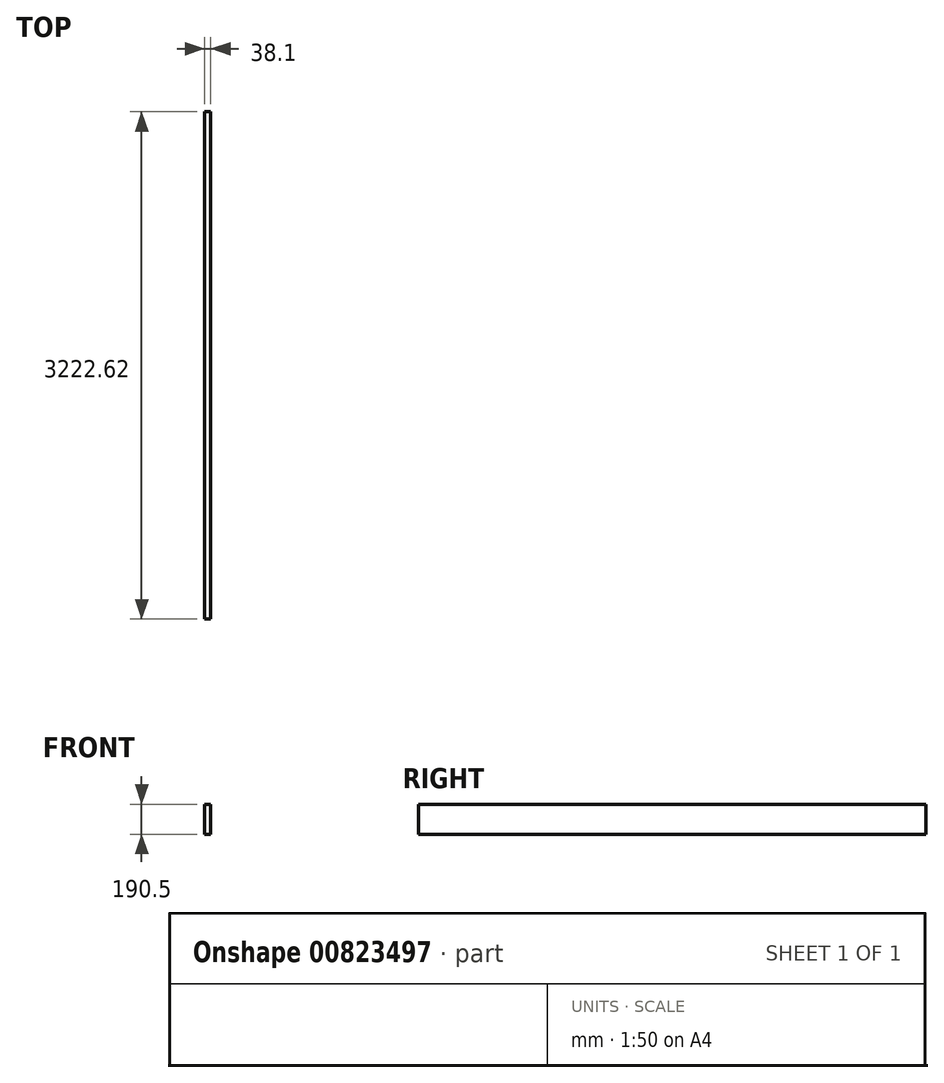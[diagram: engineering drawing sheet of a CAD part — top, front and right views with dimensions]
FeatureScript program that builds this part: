
annotation { "Feature Type Name" : "Feature", "Feature Type Description" : "" }
export const myFeature = defineFeature(function(context is Context, id is Id, definition is map)
    precondition{}
    {
        {
            var Q0;
            Q0=qCreatedBy(makeId("Front.planeOp"),FACE);
            var sketch = newSketch(context, id + "F0", { "sketchPlane" : qUnion([Q0])});
            skLineSegment(sketch, "E0.bottom", {"start": v(0, 0) * mm, "end": v(38.1, 0) * mm});
            skLineSegment(sketch, "E0.top", {"start": v(0, 190.5) * mm, "end": v(38.1, 190.5) * mm});
            skLineSegment(sketch, "E0.left", {"start": v(0, 0) * mm, "end": v(0, 190.5) * mm});
            skLineSegment(sketch, "E0.right", {"start": v(38.1, 0) * mm, "end": v(38.1, 190.5) * mm});
            skSolve(sketch);
        }
        {
            var Q0;
            Q0=qSketchRegion(id+"F0",true);
            extrude(context, id + "F1", {"entities" : qUnion([Q0]), "depth" : 3222.62 * mm, "offsetDistance" : 25.4 * mm});
        }
    });
